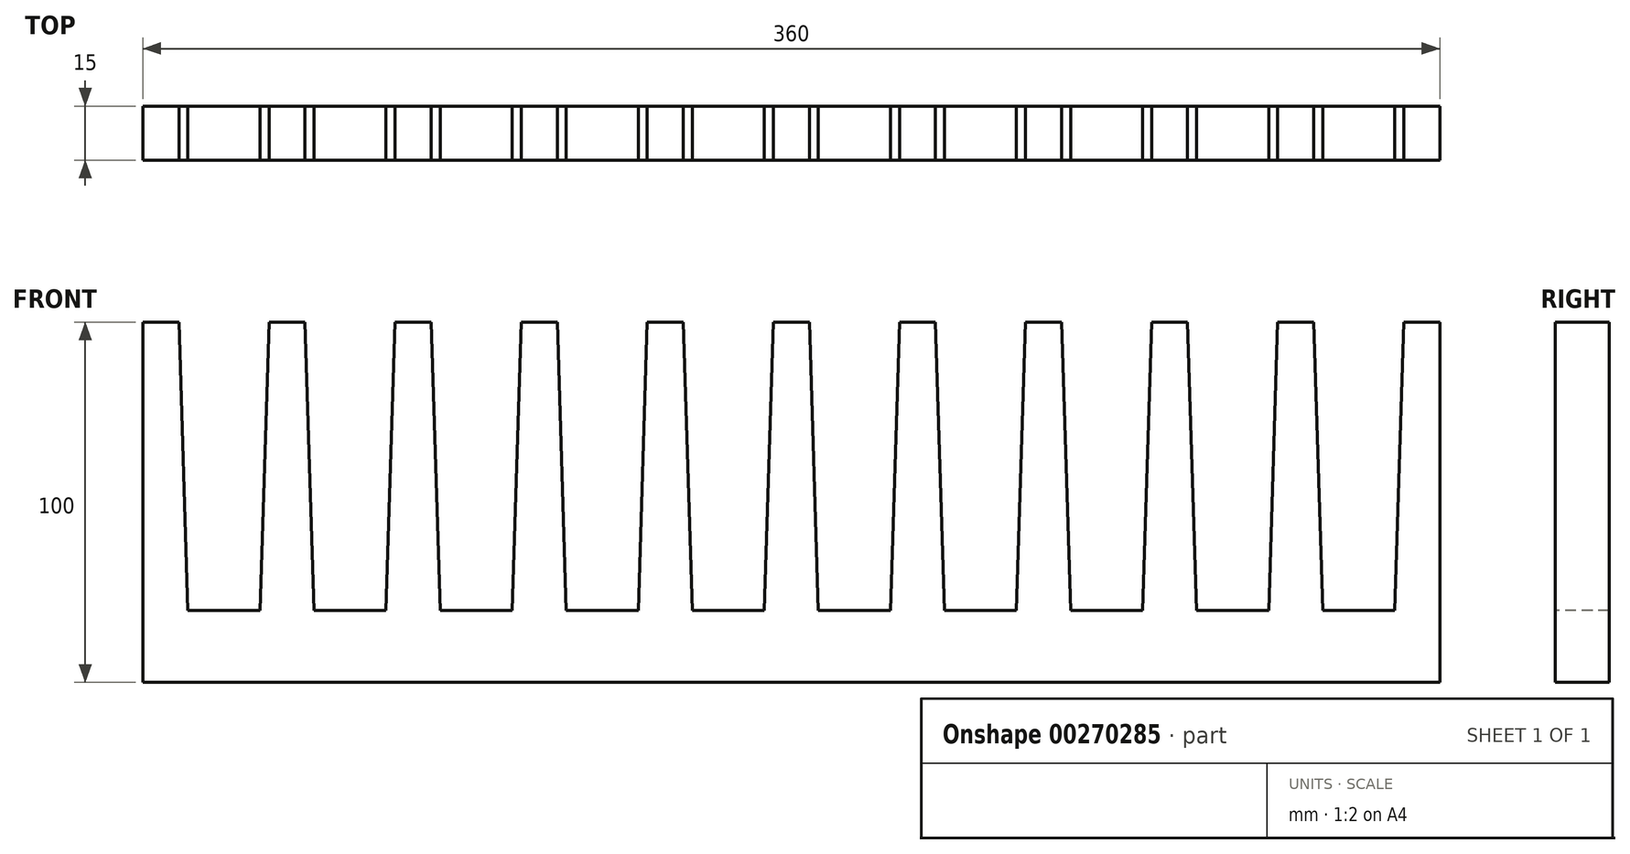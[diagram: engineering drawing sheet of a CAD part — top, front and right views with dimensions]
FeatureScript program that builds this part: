
annotation { "Feature Type Name" : "Feature", "Feature Type Description" : "" }
export const myFeature = defineFeature(function(context is Context, id is Id, definition is map)
    precondition{}
    {
        {
            var Q0;
            Q0=qCreatedBy(makeId("Front.planeOp"),FACE);
            var sketch = newSketch(context, id + "F0", { "sketchPlane" : qUnion([Q0])});
            skLineSegment(sketch, "E0.bottom", {"start": v(-192.36, 47.02) * mm, "end": v(167.64, 47.02) * mm});
            skLineSegment(sketch, "E0.top", {"start": v(-192.36, -52.98) * mm, "end": v(167.64, -52.98) * mm});
            skLineSegment(sketch, "E0.left", {"start": v(-192.36, 47.02) * mm, "end": v(-192.36, -52.98) * mm});
            skLineSegment(sketch, "E0.right", {"start": v(167.64, 47.02) * mm, "end": v(167.64, -52.98) * mm});
            skSolve(sketch);
        }
        {
            var Q0;
            Q0=makeQuery(id+"F0.imprint","IMPRINT",FACE,{"disambiguationData":[TD([[makeQuery(id+"F0.imprint","IMPRINT",EDGE,{"derivedFrom":sQuery(id+"F0.wireOp",EDGE,"E0.bottom")}),-1.0]])]});
            extrude(context, id + "F1", {"entities" : qUnion([Q0]), "depth" : 15 * mm});
        }
        {
            var Q0;
            Q0=makeQuery(id+"F1.opExtrude","CAP_FACE",FACE,{"disambiguationData":[OSD([sQuery(id+"F0.wireOp",EDGE,"E0.bottom"),sQuery(id+"F0.wireOp",EDGE,"E0.top"),sQuery(id+"F0.wireOp",EDGE,"E0.left"),sQuery(id+"F0.wireOp",EDGE,"E0.right")])],"isStart":false});
            var sketch = newSketch(context, id + "F2", { "sketchPlane" : qUnion([Q0])});
            skLineSegment(sketch, "E1", {"start": v(-192.36, 47.02) * mm, "end": v(-182.36, 47.02) * mm});
            skLineSegment(sketch, "E2", {"start": v(-182.36, 47.02) * mm, "end": v(-179.86, -32.98) * mm});
            skLineSegment(sketch, "E3", {"start": v(-179.86, -32.98) * mm, "end": v(-159.86, -32.98) * mm});
            skLineSegment(sketch, "E4", {"start": v(-159.86, -32.98) * mm, "end": v(-157.36, 47.02) * mm});
            skLineSegment(sketch, "E5", {"start": v(-192.36, -32.98) * mm, "end": v(167.64, -32.98) * mm, "construction": true});
            skLineSegment(sketch, "E6", {"start": v(-169.86, 47.02) * mm, "end": v(-169.86, -32.98) * mm, "construction": true});
            skLineSegment(sketch, "E7.1.0.0", {"start": v(-134.86, 47.02) * mm, "end": v(-134.86, -32.98) * mm, "construction": true});
            skLineSegment(sketch, "E7.1.0.1", {"start": v(-124.86, -32.98) * mm, "end": v(-122.36, 47.02) * mm});
            skLineSegment(sketch, "E7.1.0.2", {"start": v(-147.36, 47.02) * mm, "end": v(-144.86, -32.98) * mm});
            skLineSegment(sketch, "E7.1.0.3", {"start": v(-157.36, 47.02) * mm, "end": v(-147.36, 47.02) * mm});
            skLineSegment(sketch, "E7.1.0.4", {"start": v(-144.86, -32.98) * mm, "end": v(-124.86, -32.98) * mm});
            skLineSegment(sketch, "E7.2.0.0", {"start": v(-99.86, 47.02) * mm, "end": v(-99.86, -32.98) * mm, "construction": true});
            skLineSegment(sketch, "E7.2.0.1", {"start": v(-89.86, -32.98) * mm, "end": v(-87.36, 47.02) * mm});
            skLineSegment(sketch, "E7.2.0.2", {"start": v(-112.36, 47.02) * mm, "end": v(-109.86, -32.98) * mm});
            skLineSegment(sketch, "E7.2.0.3", {"start": v(-122.36, 47.02) * mm, "end": v(-112.36, 47.02) * mm});
            skLineSegment(sketch, "E7.2.0.4", {"start": v(-109.86, -32.98) * mm, "end": v(-89.86, -32.98) * mm});
            skLineSegment(sketch, "E7.3.0.0", {"start": v(-64.86, 47.02) * mm, "end": v(-64.86, -32.98) * mm, "construction": true});
            skLineSegment(sketch, "E7.3.0.1", {"start": v(-54.86, -32.98) * mm, "end": v(-52.36, 47.02) * mm});
            skLineSegment(sketch, "E7.3.0.2", {"start": v(-77.36, 47.02) * mm, "end": v(-74.86, -32.98) * mm});
            skLineSegment(sketch, "E7.3.0.3", {"start": v(-87.36, 47.02) * mm, "end": v(-77.36, 47.02) * mm});
            skLineSegment(sketch, "E7.3.0.4", {"start": v(-74.86, -32.98) * mm, "end": v(-54.86, -32.98) * mm});
            skLineSegment(sketch, "E7.4.0.0", {"start": v(-29.86, 47.02) * mm, "end": v(-29.86, -32.98) * mm, "construction": true});
            skLineSegment(sketch, "E7.4.0.1", {"start": v(-19.86, -32.98) * mm, "end": v(-17.36, 47.02) * mm});
            skLineSegment(sketch, "E7.4.0.2", {"start": v(-42.36, 47.02) * mm, "end": v(-39.86, -32.98) * mm});
            skLineSegment(sketch, "E7.4.0.3", {"start": v(-52.36, 47.02) * mm, "end": v(-42.36, 47.02) * mm});
            skLineSegment(sketch, "E7.4.0.4", {"start": v(-39.86, -32.98) * mm, "end": v(-19.86, -32.98) * mm});
            skLineSegment(sketch, "E7.5.0.0", {"start": v(5.14, 47.02) * mm, "end": v(5.14, -32.98) * mm, "construction": true});
            skLineSegment(sketch, "E7.5.0.1", {"start": v(15.14, -32.98) * mm, "end": v(17.64, 47.02) * mm});
            skLineSegment(sketch, "E7.5.0.2", {"start": v(-7.36, 47.02) * mm, "end": v(-4.86, -32.98) * mm});
            skLineSegment(sketch, "E7.5.0.3", {"start": v(-17.36, 47.02) * mm, "end": v(-7.36, 47.02) * mm});
            skLineSegment(sketch, "E7.5.0.4", {"start": v(-4.86, -32.98) * mm, "end": v(15.14, -32.98) * mm});
            skLineSegment(sketch, "E7.6.0.0", {"start": v(40.14, 47.02) * mm, "end": v(40.14, -32.98) * mm, "construction": true});
            skLineSegment(sketch, "E7.6.0.1", {"start": v(50.14, -32.98) * mm, "end": v(52.64, 47.02) * mm});
            skLineSegment(sketch, "E7.6.0.2", {"start": v(27.64, 47.02) * mm, "end": v(30.14, -32.98) * mm});
            skLineSegment(sketch, "E7.6.0.3", {"start": v(17.64, 47.02) * mm, "end": v(27.64, 47.02) * mm});
            skLineSegment(sketch, "E7.6.0.4", {"start": v(30.14, -32.98) * mm, "end": v(50.14, -32.98) * mm});
            skLineSegment(sketch, "E7.7.0.0", {"start": v(75.14, 47.02) * mm, "end": v(75.14, -32.98) * mm, "construction": true});
            skLineSegment(sketch, "E7.7.0.1", {"start": v(85.14, -32.98) * mm, "end": v(87.64, 47.02) * mm});
            skLineSegment(sketch, "E7.7.0.2", {"start": v(62.64, 47.02) * mm, "end": v(65.14, -32.98) * mm});
            skLineSegment(sketch, "E7.7.0.3", {"start": v(52.64, 47.02) * mm, "end": v(62.64, 47.02) * mm});
            skLineSegment(sketch, "E7.7.0.4", {"start": v(65.14, -32.98) * mm, "end": v(85.14, -32.98) * mm});
            skLineSegment(sketch, "E7.8.0.0", {"start": v(110.14, 47.02) * mm, "end": v(110.14, -32.98) * mm, "construction": true});
            skLineSegment(sketch, "E7.8.0.1", {"start": v(120.14, -32.98) * mm, "end": v(122.64, 47.02) * mm});
            skLineSegment(sketch, "E7.8.0.2", {"start": v(97.64, 47.02) * mm, "end": v(100.14, -32.98) * mm});
            skLineSegment(sketch, "E7.8.0.3", {"start": v(87.64, 47.02) * mm, "end": v(97.64, 47.02) * mm});
            skLineSegment(sketch, "E7.8.0.4", {"start": v(100.14, -32.98) * mm, "end": v(120.14, -32.98) * mm});
            skLineSegment(sketch, "E7.9.0.0", {"start": v(145.14, 47.02) * mm, "end": v(145.14, -32.98) * mm, "construction": true});
            skLineSegment(sketch, "E7.9.0.1", {"start": v(155.14, -32.98) * mm, "end": v(157.64, 47.02) * mm});
            skLineSegment(sketch, "E7.9.0.2", {"start": v(132.64, 47.02) * mm, "end": v(135.14, -32.98) * mm});
            skLineSegment(sketch, "E7.9.0.3", {"start": v(122.64, 47.02) * mm, "end": v(132.64, 47.02) * mm});
            skLineSegment(sketch, "E7.9.0.4", {"start": v(135.14, -32.98) * mm, "end": v(155.14, -32.98) * mm});
            skLineSegment(sketch, "E7.direction1", {"start": v(-179.86, -32.98) * mm, "end": v(-144.86, -32.98) * mm, "construction": true});
            skLineSegment(sketch, "E8", {"start": v(-192.36, 47.02) * mm, "end": v(-192.36, -52.98) * mm});
            skLineSegment(sketch, "E9", {"start": v(-192.36, -52.98) * mm, "end": v(167.64, -52.98) * mm});
            skLineSegment(sketch, "E10", {"start": v(167.64, -52.98) * mm, "end": v(167.64, 47.02) * mm});
            skLineSegment(sketch, "E11", {"start": v(167.64, 47.02) * mm, "end": v(157.64, 47.02) * mm});
            skSolve(sketch);
        }
        {
            var Q0;
            Q0 = qSketchRegion(id + "F2", true);
            extrude(context, id + "F3", {"entities" : qUnion([Q0]), "operationType" : NewBodyOperationType.INTERSECT, "endBound" : BoundingType.UP_TO_NEXT, "oppositeDirection" : true, "depth" : 25 * mm});
        }
    });
